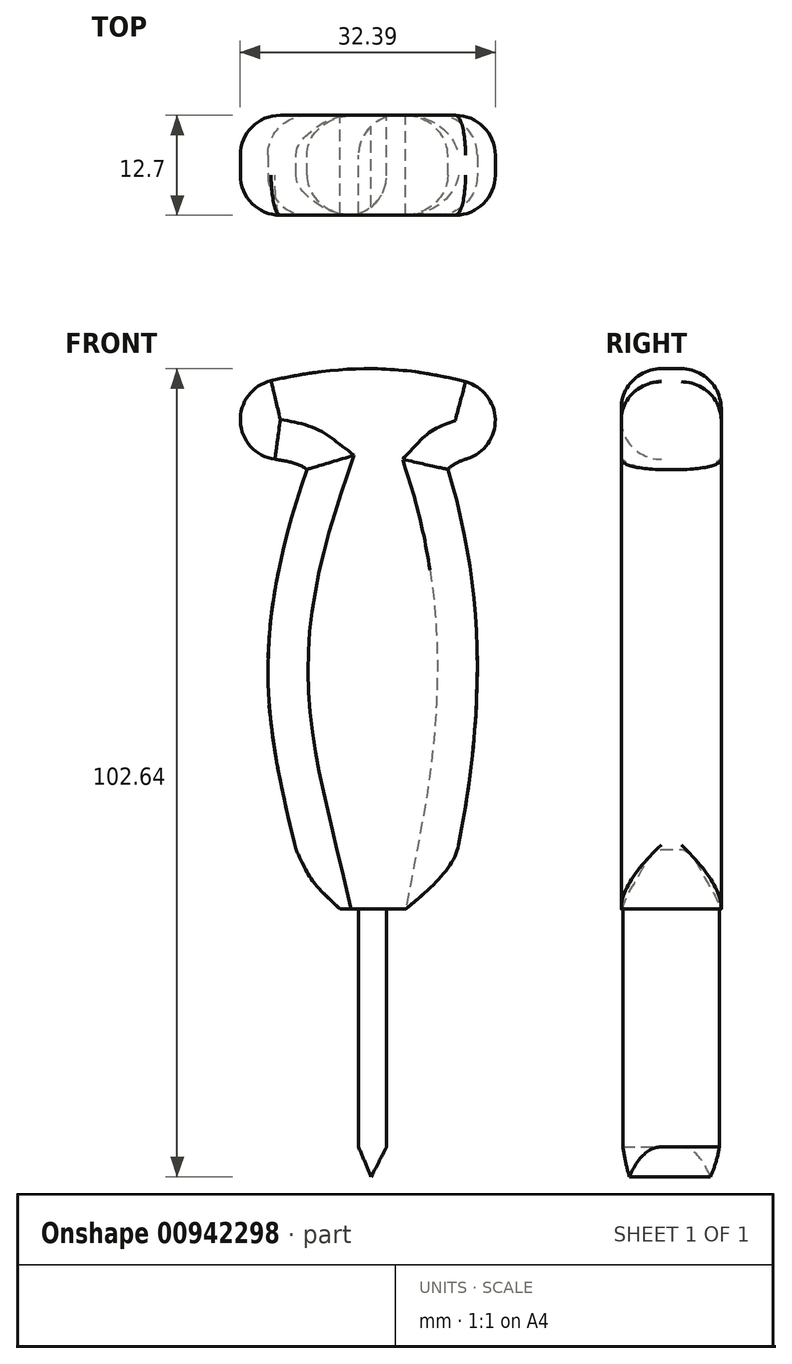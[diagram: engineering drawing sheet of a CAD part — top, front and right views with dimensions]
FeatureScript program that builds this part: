
annotation { "Feature Type Name" : "Feature", "Feature Type Description" : "" }
export const myFeature = defineFeature(function(context is Context, id is Id, definition is map)
    precondition{}
    {
        {
            var Q0;
            Q0=qCreatedBy(makeId("Front.planeOp"),FACE);
            var sketch = newSketch(context, id + "F0", { "sketchPlane" : qUnion([Q0])});
            skFitSpline(sketch, "E0", {"points": [v(-16.15, 41.26) * mm, v(-4.22, 32.11) * mm], "startDerivative": vector(-14.31, -29.81) * mm, "endDerivative": vector(11.93, -9.14) * mm});
            skFitSpline(sketch, "E1", {"points": [v(22.01, 41.26) * mm, v(13.67, 32.11) * mm], "startDerivative": vector(11.33, -25.04) * mm, "endDerivative": vector(-8.35, -9.14) * mm});
            skFitSpline(sketch, "E2", {"points": [v(-16.15, 41.26) * mm, v(22.01, 41.26) * mm], "startDerivative": vector(42.34, 14.31) * mm, "endDerivative": vector(38.76, -14.9) * mm});
            skFitSpline(sketch, "E3", {"points": [v(-4.22, 32.11) * mm, v(-5.61, -16.19) * mm], "startDerivative": vector(-23.25, -67.38) * mm, "endDerivative": vector(10.73, -45.32) * mm});
            skFitSpline(sketch, "E4", {"points": [v(13.67, 32.11) * mm, v(15.06, -15.59) * mm], "startDerivative": vector(15.5, -50.09) * mm, "endDerivative": vector(-8.94, -46.77) * mm});
            skFitSpline(sketch, "E5", {"points": [v(15.06, -15.59) * mm, v(8.3, -23.74) * mm], "startDerivative": vector(-1.79, -8.94) * mm, "endDerivative": vector(-8.94, -7.16) * mm});
            skFitSpline(sketch, "E6", {"points": [v(-5.61, -16.19) * mm, v(0, -23.74) * mm], "startDerivative": vector(5.96, -12.52) * mm, "endDerivative": vector(10.88, -10.14) * mm});
            skLineSegment(sketch, "E7", {"start": v(0, -23.74) * mm, "end": v(8.3, -23.74) * mm});
            skLineSegment(sketch, "E8", {"start": v(2.34, -23.74) * mm, "end": v(2.34, -53.95) * mm});
            skLineSegment(sketch, "E9", {"start": v(5.91, -23.74) * mm, "end": v(5.91, -53.95) * mm});
            skLineSegment(sketch, "E10", {"start": v(2.34, -53.95) * mm, "end": v(3.93, -57.73) * mm});
            skLineSegment(sketch, "E11", {"start": v(3.93, -57.73) * mm, "end": v(5.91, -53.95) * mm});
            skSolve(sketch);
        }
        {
            var Q0;
            {var subQ1=sQuery(id+"F0.wireOp",EDGE,"E8");Q0=makeQuery(id+"F0.imprint","IMPRINT",FACE,{"disambiguationData":[TD([[makeQuery(id+"F0.imprint","IMPRINT",EDGE,{"derivedFrom":subQ1}),1.0]])]});}
            var Q1;
            Q1=makeQuery(id+"F0.imprint","IMPRINT",FACE,{"disambiguationData":[TD([[makeQuery(id+"F0.imprint","IMPRINT",EDGE,{"derivedFrom":sQuery(id+"F0.wireOp",EDGE,"E0")}),1.0]])]});
            extrude(context, id + "F1", {"entities" : qUnion([Q0, Q1]), "depth" : 12.7 * mm, "offsetDistance" : 25.4 * mm});
        }
        {
            var Q0;
            Q0=makeQuery(id+"F1.opExtrude","CAP_EDGE",EDGE,{"disambiguationData":[OSD([sQuery(id+"F0.wireOp",EDGE,"E2")])],"isStart":false});
            var Q1;
            Q1=makeQuery(id+"F1.opExtrude","SWEPT_EDGE",EDGE,{"disambiguationData":[OSD([sQuery(id+"F0.wireOp",EDGE,"E0"),sQuery(id+"F0.wireOp",EDGE,"E2")])]});
            var Q2;
            Q2=makeQuery(id+"F1.opExtrude","CAP_EDGE",EDGE,{"disambiguationData":[OSD([sQuery(id+"F0.wireOp",EDGE,"E4")])],"isStart":false});
            var Q3;
            Q3=makeQuery(id+"F1.opExtrude","CAP_EDGE",EDGE,{"disambiguationData":[OSD([sQuery(id+"F0.wireOp",EDGE,"E4")])],"isStart":true});
            var Q4;
            Q4=makeQuery(id+"F1.opExtrude","CAP_EDGE",EDGE,{"disambiguationData":[OSD([sQuery(id+"F0.wireOp",EDGE,"E9")])],"isStart":false});
            var Q5;
            Q5=makeQuery(id+"F1.opExtrude","CAP_EDGE",EDGE,{"disambiguationData":[OSD([sQuery(id+"F0.wireOp",EDGE,"E3")])],"isStart":true});
            fillet(context, id + "F2", {"entities" : qUnion([Q0, Q1, Q2, Q3, Q4, Q5]), "radius" : 5.08 * mm, "tangentPropagation" : true, "allowEdgeOverflow" : false});
        }
        {
            var Q0;
            Q0=makeQuery(id+"F1.opExtrude","CAP_EDGE",EDGE,{"disambiguationData":[OSD([sQuery(id+"F0.wireOp",EDGE,"E3")])],"isStart":false});
            var Q1;
            {var subQ0=sQuery(id+"F0.wireOp",EDGE,"E2");Q1=makeQuery(id+"F2.opFillet","BLEND_EDGE",EDGE,{"blendedFrom":[makeQuery(id+"F1.opExtrude","CAP_EDGE",EDGE,{"disambiguationData":[OSD([subQ0])],"isStart":false}),makeQuery(id+"F1.opExtrude","SWEPT_FACE",FACE,{"disambiguationData":[OSD([subQ0])]})],"blendedInto":[makeQuery(id+"F1.opExtrude","SWEPT_FACE",FACE,{"disambiguationData":[OSD([subQ0])]})]});}
            var Q2;
            Q2=makeQuery(id+"F1.opExtrude","CAP_EDGE",EDGE,{"disambiguationData":[OSD([sQuery(id+"F0.wireOp",EDGE,"E2")])],"isStart":true});
            fillet(context, id + "F3", {"entities" : qUnion([Q0, Q1, Q2]), "radius" : 5.08 * mm, "tangentPropagation" : true, "allowEdgeOverflow" : false});
        }
        {
            var Q0;
            Q0=makeQuery(id+"F3.opFillet","BLEND_EDGE",EDGE,{"blendedFrom":[makeQuery(id+"F1.opExtrude","CAP_EDGE",EDGE,{"disambiguationData":[OSD([sQuery(id+"F0.wireOp",EDGE,"E2")])],"isStart":true}),makeQuery(id+"F1.opExtrude","SWEPT_FACE",FACE,{"disambiguationData":[OSD([sQuery(id+"F0.wireOp",EDGE,"E1")])]})],"blendedInto":[makeQuery(id+"F1.opExtrude","SWEPT_FACE",FACE,{"disambiguationData":[OSD([sQuery(id+"F0.wireOp",EDGE,"E1")])]})]});
            var Q1;
            {var subQ0=sQuery(id+"F0.wireOp",EDGE,"E2");Q1=makeQuery(id+"F2.opFillet","BLEND_EDGE",EDGE,{"blendedFrom":[makeQuery(id+"F1.opExtrude","SWEPT_EDGE",EDGE,{"disambiguationData":[OSD([sQuery(id+"F0.wireOp",EDGE,"E0"),subQ0])]}),makeQuery(id+"F1.opExtrude","CAP_EDGE",EDGE,{"disambiguationData":[OSD([subQ0])],"isStart":false})],"blendedInto":[]});}
            fillet(context, id + "F4", {"entities" : qUnion([Q0, Q1]), "radius" : 5.08 * mm, "tangentPropagation" : true, "allowEdgeOverflow" : false});
        }
        {
            var Q0;
            Q0=makeQuery(id+"F1.opExtrude","CAP_EDGE",EDGE,{"disambiguationData":[OSD([sQuery(id+"F0.wireOp",EDGE,"E8")])],"isStart":true});
            fillet(context, id + "F5", {"entities" : qUnion([Q0]), "radius" : 5.08 * mm, "tangentPropagation" : true, "allowEdgeOverflow" : false});
        }
    });
